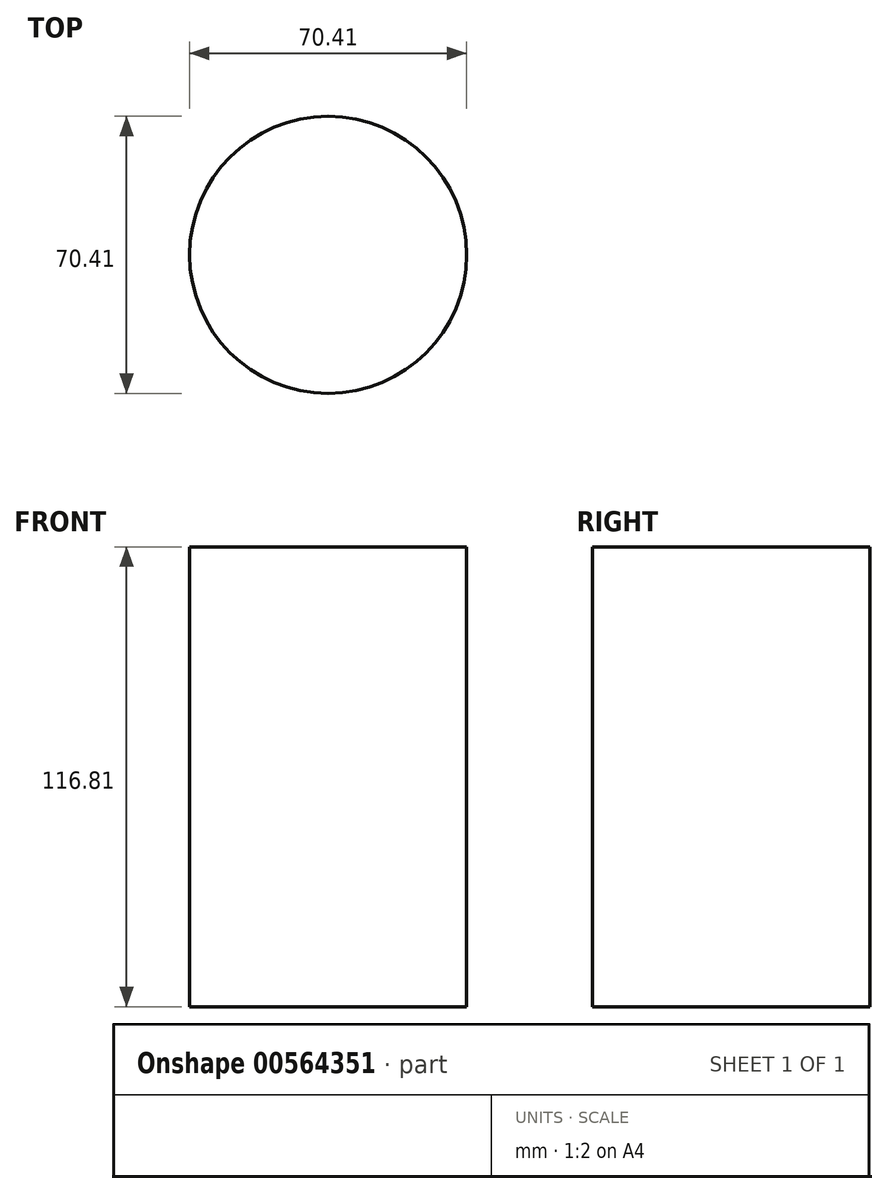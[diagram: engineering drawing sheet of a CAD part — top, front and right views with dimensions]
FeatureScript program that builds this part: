
annotation { "Feature Type Name" : "Feature", "Feature Type Description" : "" }
export const myFeature = defineFeature(function(context is Context, id is Id, definition is map)
    precondition{}
    {
        {
            var Q0;
            Q0=qCreatedBy(makeId("Top.planeOp"),FACE);
            var sketch = newSketch(context, id + "F0", { "sketchPlane" : qUnion([Q0])});
            skCircle(sketch, "E0", {"center": v(21.64, 29.6) * mm, "radius": 35.2 * mm});
            skSolve(sketch);
        }
        {
            var Q0;
            Q0=makeQuery(id+"F0.imprint","IMPRINT",FACE,{"disambiguationData":[TD([[makeQuery(id+"F0.imprint","IMPRINT",EDGE,{"derivedFrom":sQuery(id+"F0.wireOp",EDGE,"E0")}),1.0]])]});
            extrude(context, id + "F1", {"entities" : qUnion([Q0]), "depth" : 116.8 * mm, "offsetDistance" : 25 * mm});
        }
    });
